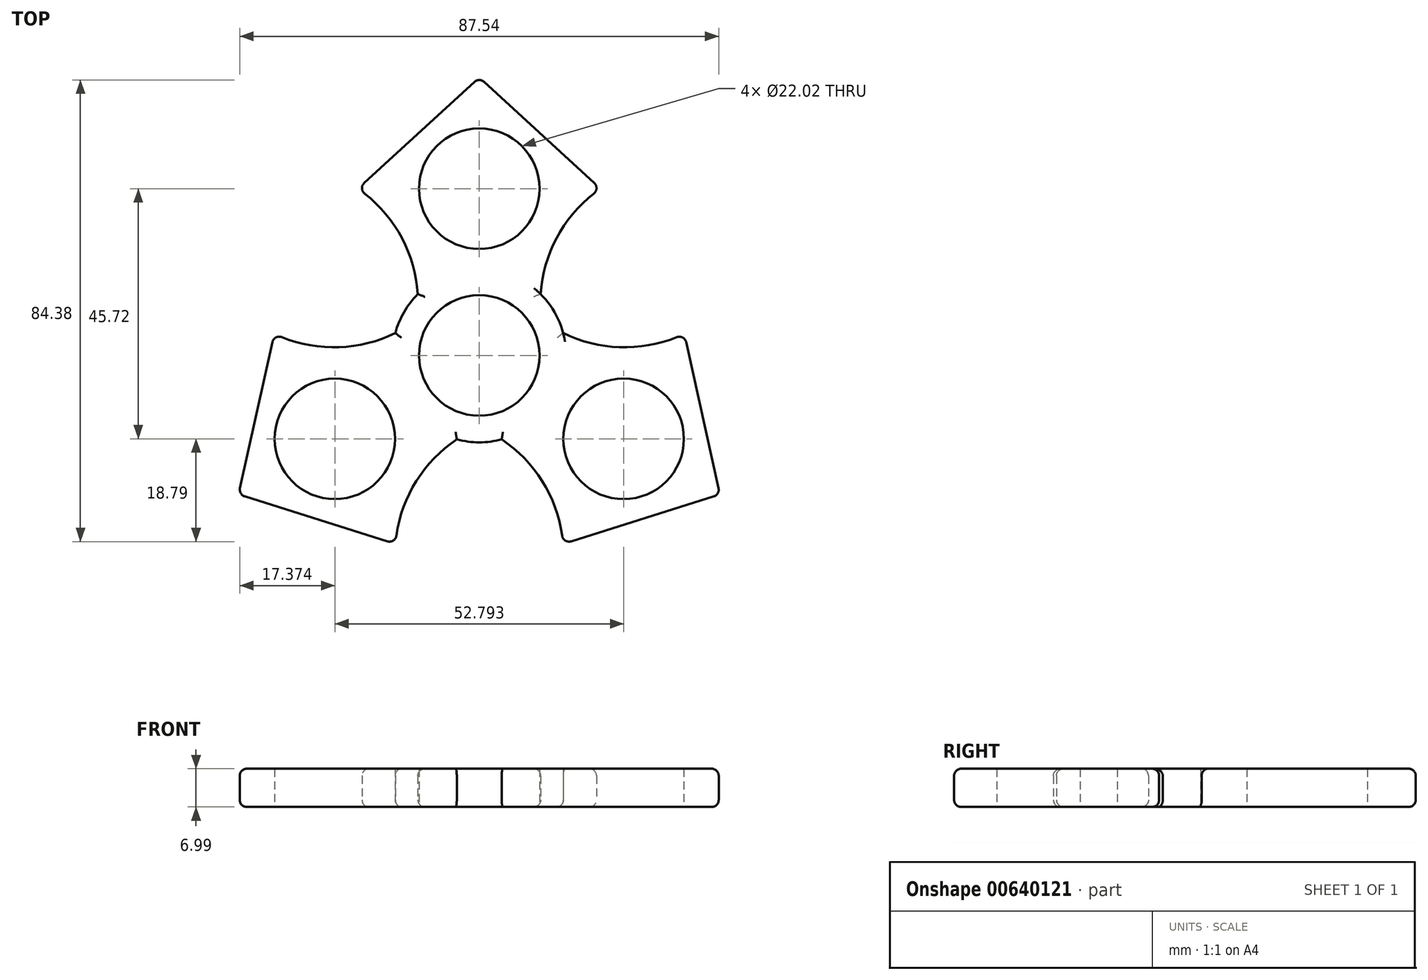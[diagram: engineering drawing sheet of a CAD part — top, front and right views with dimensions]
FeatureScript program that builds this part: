
annotation { "Feature Type Name" : "Feature", "Feature Type Description" : "" }
export const myFeature = defineFeature(function(context is Context, id is Id, definition is map)
    precondition{}
    {
        {
            var Q0;
            Q0=qCreatedBy(makeId("Top.planeOp"),FACE);
            var sketch = newSketch(context, id + "F0", { "sketchPlane" : qUnion([Q0])});
            skCircle(sketch, "E0", {"center": v(0, 0) * mm, "radius": 11.01 * mm});
            skLineSegment(sketch, "E1", {"start": v(0, 0) * mm, "end": v(0, 30.48) * mm});
            skLineSegment(sketch, "E2", {"start": v(0, 0) * mm, "end": v(26.4, -15.24) * mm});
            skLineSegment(sketch, "E3", {"start": v(0, 0) * mm, "end": v(-26.4, -15.24) * mm});
            skCircle(sketch, "E4", {"center": v(0, 30.48) * mm, "radius": 11.01 * mm});
            skCircle(sketch, "E5", {"center": v(-26.4, -15.24) * mm, "radius": 11.01 * mm});
            skCircle(sketch, "E6", {"center": v(26.4, -15.24) * mm, "radius": 11.01 * mm});
            skLineSegment(sketch, "E7", {"start": v(0, 0) * mm, "end": v(0, 50.8) * mm});
            skLineSegment(sketch, "E8", {"start": v(-22.16, 30.48) * mm, "end": v(22.16, 30.48) * mm});
            skLineSegment(sketch, "E9", {"start": v(-22.16, 30.48) * mm, "end": v(0, 50.8) * mm});
            skLineSegment(sketch, "E10", {"start": v(0, 50.8) * mm, "end": v(22.16, 30.48) * mm});
            skCircle(sketch, "E11", {"center": v(0, 0) * mm, "radius": 15.88 * mm});
            skLineSegment(sketch, "E12", {"start": v(0, 0) * mm, "end": v(11.23, 11.23) * mm});
            skLineSegment(sketch, "E13", {"start": v(0, 0) * mm, "end": v(-11.23, 11.23) * mm});
            skArc(sketch, "E14", {"start": v(-11.23, 11.23) * mm, "mid": v(-14.48, 22.1) * mm, "end": v(-22.16, 30.48) * mm});
            skArc(sketch, "E15", {"start": v(22.16, 30.48) * mm, "mid": v(14.48, 22.1) * mm, "end": v(11.23, 11.23) * mm});
            skArc(sketch, "E16.1.0", {"start": v(-4.1, -15.33) * mm, "mid": v(-11.9, -23.6) * mm, "end": v(-15.32, -34.43) * mm});
            skLineSegment(sketch, "E16.1.1", {"start": v(-15.32, -34.43) * mm, "end": v(-44, -25.4) * mm});
            skLineSegment(sketch, "E16.1.2", {"start": v(-44, -25.4) * mm, "end": v(-37.48, 3.95) * mm});
            skLineSegment(sketch, "E16.1.3", {"start": v(-15.32, -34.43) * mm, "end": v(-37.48, 3.95) * mm});
            skArc(sketch, "E16.1.4", {"start": v(-37.48, 3.95) * mm, "mid": v(-26.39, 1.5) * mm, "end": v(-15.33, 4.1) * mm});
            skLineSegment(sketch, "E16.1.5", {"start": v(0, 0) * mm, "end": v(-15.33, 4.1) * mm});
            skLineSegment(sketch, "E16.1.6", {"start": v(0, 0) * mm, "end": v(-4.1, -15.33) * mm});
            skLineSegment(sketch, "E16.1.7", {"start": v(0, 0) * mm, "end": v(-44, -25.4) * mm});
            skArc(sketch, "E16.2.0", {"start": v(15.33, 4.1) * mm, "mid": v(26.39, 1.5) * mm, "end": v(37.48, 3.95) * mm});
            skLineSegment(sketch, "E16.2.1", {"start": v(37.48, 3.95) * mm, "end": v(44, -25.4) * mm});
            skLineSegment(sketch, "E16.2.2", {"start": v(44, -25.4) * mm, "end": v(15.32, -34.43) * mm});
            skLineSegment(sketch, "E16.2.3", {"start": v(37.48, 3.95) * mm, "end": v(15.32, -34.43) * mm});
            skArc(sketch, "E16.2.4", {"start": v(15.32, -34.43) * mm, "mid": v(11.9, -23.6) * mm, "end": v(4.1, -15.33) * mm});
            skLineSegment(sketch, "E16.2.5", {"start": v(0, 0) * mm, "end": v(4.1, -15.33) * mm});
            skLineSegment(sketch, "E16.2.6", {"start": v(0, 0) * mm, "end": v(15.33, 4.1) * mm});
            skLineSegment(sketch, "E16.2.7", {"start": v(0, 0) * mm, "end": v(44, -25.4) * mm});
            skSolve(sketch);
        }
        {
            var Q0;
            Q0 = qSketchRegion(id + "F0", true);
            extrude(context, id + "F1", {"entities" : qUnion([Q0]), "depth" : 7 * mm, "offsetDistance" : 25.4 * mm});
        }
        {
            var Q0;
            Q0=makeQuery(id+"F1.opExtrude","SWEPT_EDGE",EDGE,{"disambiguationData":[OSD([sQuery(id+"F0.wireOp",EDGE,"E8"),sQuery(id+"F0.wireOp",EDGE,"E10"),sQuery(id+"F0.wireOp",EDGE,"E15")])]});
            var Q1;
            Q1=makeQuery(id+"F1.opExtrude","SWEPT_EDGE",EDGE,{"disambiguationData":[OSD([sQuery(id+"F0.wireOp",EDGE,"E7"),sQuery(id+"F0.wireOp",EDGE,"E9"),sQuery(id+"F0.wireOp",EDGE,"E10")])]});
            var Q2;
            Q2=makeQuery(id+"F1.opExtrude","SWEPT_EDGE",EDGE,{"disambiguationData":[OSD([sQuery(id+"F0.wireOp",EDGE,"E8"),sQuery(id+"F0.wireOp",EDGE,"E9"),sQuery(id+"F0.wireOp",EDGE,"E14")])]});
            var Q3;
            Q3=makeQuery(id+"F1.opExtrude","SWEPT_EDGE",EDGE,{"disambiguationData":[OSD([sQuery(id+"F0.wireOp",EDGE,"E16.2.0"),sQuery(id+"F0.wireOp",EDGE,"E16.2.1"),sQuery(id+"F0.wireOp",EDGE,"E16.2.3")])]});
            var Q4;
            Q4=makeQuery(id+"F1.opExtrude","SWEPT_EDGE",EDGE,{"disambiguationData":[OSD([sQuery(id+"F0.wireOp",EDGE,"E16.2.1"),sQuery(id+"F0.wireOp",EDGE,"E16.2.2"),sQuery(id+"F0.wireOp",EDGE,"E16.2.7")])]});
            var Q5;
            Q5=makeQuery(id+"F1.opExtrude","SWEPT_EDGE",EDGE,{"disambiguationData":[OSD([sQuery(id+"F0.wireOp",EDGE,"E16.2.2"),sQuery(id+"F0.wireOp",EDGE,"E16.2.3"),sQuery(id+"F0.wireOp",EDGE,"E16.2.4")])]});
            var Q6;
            Q6=makeQuery(id+"F1.opExtrude","SWEPT_EDGE",EDGE,{"disambiguationData":[OSD([sQuery(id+"F0.wireOp",EDGE,"E16.1.0"),sQuery(id+"F0.wireOp",EDGE,"E16.1.1"),sQuery(id+"F0.wireOp",EDGE,"E16.1.3")])]});
            var Q7;
            Q7=makeQuery(id+"F1.opExtrude","SWEPT_EDGE",EDGE,{"disambiguationData":[OSD([sQuery(id+"F0.wireOp",EDGE,"E16.1.1"),sQuery(id+"F0.wireOp",EDGE,"E16.1.2"),sQuery(id+"F0.wireOp",EDGE,"E16.1.7")])]});
            var Q8;
            Q8=makeQuery(id+"F1.opExtrude","SWEPT_EDGE",EDGE,{"disambiguationData":[OSD([sQuery(id+"F0.wireOp",EDGE,"E16.1.2"),sQuery(id+"F0.wireOp",EDGE,"E16.1.3"),sQuery(id+"F0.wireOp",EDGE,"E16.1.4")])]});
            fillet(context, id + "F2", {"entities" : qUnion([Q0, Q1, Q2, Q3, Q4, Q5, Q6, Q7, Q8]), "radius" : 1.27 * mm, "tangentPropagation" : true, "allowEdgeOverflow" : false});
        }
        {
            var Q0;
            Q0=makeQuery(id+"F1.opExtrude","CAP_EDGE",EDGE,{"disambiguationData":[OSD([sQuery(id+"F0.wireOp",EDGE,"E9")])],"isStart":false});
            var Q1;
            Q1=makeQuery(id+"F1.opExtrude","CAP_EDGE",EDGE,{"disambiguationData":[OSD([sQuery(id+"F0.wireOp",EDGE,"E16.1.0")])],"isStart":false});
            var Q2;
            Q2=makeQuery(id+"F1.opExtrude","CAP_EDGE",EDGE,{"disambiguationData":[OSD([sQuery(id+"F0.wireOp",EDGE,"E16.1.1")])],"isStart":false});
            var Q3;
            Q3=makeQuery(id+"F1.opExtrude","CAP_EDGE",EDGE,{"disambiguationData":[OSD([sQuery(id+"F0.wireOp",EDGE,"E16.1.2")])],"isStart":false});
            var Q4;
            Q4=makeQuery(id+"F1.opExtrude","CAP_EDGE",EDGE,{"disambiguationData":[OSD([sQuery(id+"F0.wireOp",EDGE,"E16.1.4")])],"isStart":false});
            var Q5;
            {var subQ0=sQuery(id+"F0.wireOp",EDGE,"E11");Q5=makeQuery(id+"F1.opExtrude","CAP_EDGE",EDGE,{"disambiguationData":[OSD([subQ0]),TDD([makeQuery(id+"F0.imprint","IMPRINT",EDGE,{"disambiguationData":[TD([[makeQuery(id+"F0.imprint","INTERSECT",VERTEX,{"derivedFrom":[subQ0,sQuery(id+"F0.wireOp",EDGE,"E13"),sQuery(id+"F0.wireOp",EDGE,"E14")]}),-1.0]])],"derivedFrom":subQ0})])],"isStart":false});}
            var Q6;
            Q6=makeQuery(id+"F1.opExtrude","CAP_EDGE",EDGE,{"disambiguationData":[OSD([sQuery(id+"F0.wireOp",EDGE,"E14")])],"isStart":false});
            var Q7;
            Q7=makeQuery(id+"F1.opExtrude","CAP_EDGE",EDGE,{"disambiguationData":[OSD([sQuery(id+"F0.wireOp",EDGE,"E10")])],"isStart":false});
            var Q8;
            Q8=makeQuery(id+"F1.opExtrude","CAP_EDGE",EDGE,{"disambiguationData":[OSD([sQuery(id+"F0.wireOp",EDGE,"E15")])],"isStart":false});
            var Q9;
            Q9=makeQuery(id+"F1.opExtrude","CAP_EDGE",EDGE,{"disambiguationData":[OSD([sQuery(id+"F0.wireOp",EDGE,"E16.2.0")])],"isStart":false});
            var Q10;
            Q10=makeQuery(id+"F1.opExtrude","CAP_EDGE",EDGE,{"disambiguationData":[OSD([sQuery(id+"F0.wireOp",EDGE,"E16.2.1")])],"isStart":false});
            var Q11;
            Q11=makeQuery(id+"F1.opExtrude","CAP_EDGE",EDGE,{"disambiguationData":[OSD([sQuery(id+"F0.wireOp",EDGE,"E16.2.2")])],"isStart":false});
            var Q12;
            Q12=makeQuery(id+"F1.opExtrude","CAP_EDGE",EDGE,{"disambiguationData":[OSD([sQuery(id+"F0.wireOp",EDGE,"E16.2.4")])],"isStart":false});
            var Q13;
            {var subQ0=sQuery(id+"F0.wireOp",EDGE,"E11");Q13=makeQuery(id+"F1.opExtrude","CAP_EDGE",EDGE,{"disambiguationData":[OSD([subQ0]),TDD([makeQuery(id+"F0.imprint","IMPRINT",EDGE,{"disambiguationData":[TD([[makeQuery(id+"F0.imprint","INTERSECT",VERTEX,{"derivedFrom":[subQ0,sQuery(id+"F0.wireOp",EDGE,"E16.1.0"),sQuery(id+"F0.wireOp",EDGE,"E16.1.6")]}),-1.0]])],"derivedFrom":subQ0})])],"isStart":false});}
            var Q14;
            Q14=makeQuery(id+"F1.opExtrude","CAP_EDGE",EDGE,{"disambiguationData":[OSD([sQuery(id+"F0.wireOp",EDGE,"E16.1.1")])],"isStart":true});
            var Q15;
            Q15=makeQuery(id+"F1.opExtrude","CAP_EDGE",EDGE,{"disambiguationData":[OSD([sQuery(id+"F0.wireOp",EDGE,"E16.1.2")])],"isStart":true});
            var Q16;
            Q16=makeQuery(id+"F1.opExtrude","CAP_EDGE",EDGE,{"disambiguationData":[OSD([sQuery(id+"F0.wireOp",EDGE,"E16.1.4")])],"isStart":true});
            var Q17;
            {var subQ0=sQuery(id+"F0.wireOp",EDGE,"E11");Q17=makeQuery(id+"F1.opExtrude","CAP_EDGE",EDGE,{"disambiguationData":[OSD([subQ0]),TDD([makeQuery(id+"F0.imprint","IMPRINT",EDGE,{"disambiguationData":[TD([[makeQuery(id+"F0.imprint","INTERSECT",VERTEX,{"derivedFrom":[subQ0,sQuery(id+"F0.wireOp",EDGE,"E13"),sQuery(id+"F0.wireOp",EDGE,"E14")]}),-1.0]])],"derivedFrom":subQ0})])],"isStart":true});}
            var Q18;
            Q18=makeQuery(id+"F1.opExtrude","CAP_EDGE",EDGE,{"disambiguationData":[OSD([sQuery(id+"F0.wireOp",EDGE,"E14")])],"isStart":true});
            var Q19;
            Q19=makeQuery(id+"F1.opExtrude","CAP_EDGE",EDGE,{"disambiguationData":[OSD([sQuery(id+"F0.wireOp",EDGE,"E9")])],"isStart":true});
            var Q20;
            Q20=makeQuery(id+"F1.opExtrude","CAP_EDGE",EDGE,{"disambiguationData":[OSD([sQuery(id+"F0.wireOp",EDGE,"E10")])],"isStart":true});
            var Q21;
            Q21=makeQuery(id+"F1.opExtrude","CAP_EDGE",EDGE,{"disambiguationData":[OSD([sQuery(id+"F0.wireOp",EDGE,"E15")])],"isStart":true});
            var Q22;
            {var subQ0=sQuery(id+"F0.wireOp",EDGE,"E11");Q22=makeQuery(id+"F1.opExtrude","CAP_EDGE",EDGE,{"disambiguationData":[OSD([subQ0]),TDD([makeQuery(id+"F0.imprint","IMPRINT",EDGE,{"disambiguationData":[TD([[makeQuery(id+"F0.imprint","INTERSECT",VERTEX,{"derivedFrom":[subQ0,sQuery(id+"F0.wireOp",EDGE,"E12"),sQuery(id+"F0.wireOp",EDGE,"E15")]}),1.0]])],"derivedFrom":subQ0})])],"isStart":true});}
            var Q23;
            Q23=makeQuery(id+"F1.opExtrude","CAP_EDGE",EDGE,{"disambiguationData":[OSD([sQuery(id+"F0.wireOp",EDGE,"E16.2.0")])],"isStart":true});
            var Q24;
            Q24=makeQuery(id+"F1.opExtrude","CAP_EDGE",EDGE,{"disambiguationData":[OSD([sQuery(id+"F0.wireOp",EDGE,"E16.2.1")])],"isStart":true});
            var Q25;
            Q25=makeQuery(id+"F1.opExtrude","CAP_EDGE",EDGE,{"disambiguationData":[OSD([sQuery(id+"F0.wireOp",EDGE,"E16.2.2")])],"isStart":true});
            var Q26;
            Q26=makeQuery(id+"F1.opExtrude","CAP_EDGE",EDGE,{"disambiguationData":[OSD([sQuery(id+"F0.wireOp",EDGE,"E16.2.4")])],"isStart":true});
            var Q27;
            {var subQ0=sQuery(id+"F0.wireOp",EDGE,"E11");Q27=makeQuery(id+"F1.opExtrude","CAP_EDGE",EDGE,{"disambiguationData":[OSD([subQ0]),TDD([makeQuery(id+"F0.imprint","IMPRINT",EDGE,{"disambiguationData":[TD([[makeQuery(id+"F0.imprint","INTERSECT",VERTEX,{"derivedFrom":[subQ0,sQuery(id+"F0.wireOp",EDGE,"E16.1.0"),sQuery(id+"F0.wireOp",EDGE,"E16.1.6")]}),-1.0]])],"derivedFrom":subQ0})])],"isStart":true});}
            var Q28;
            Q28=makeQuery(id+"F1.opExtrude","CAP_EDGE",EDGE,{"disambiguationData":[OSD([sQuery(id+"F0.wireOp",EDGE,"E16.1.0")])],"isStart":true});
            fillet(context, id + "F3", {"entities" : qUnion([Q0, Q1, Q2, Q3, Q4, Q5, Q6, Q7, Q8, Q9, Q10, Q11, Q12, Q13, Q14, Q15, Q16, Q17, Q18, Q19, Q20, Q21, Q22, Q23, Q24, Q25, Q26, Q27, Q28]), "radius" : 1.27 * mm, "tangentPropagation" : true, "allowEdgeOverflow" : false});
        }
    });
